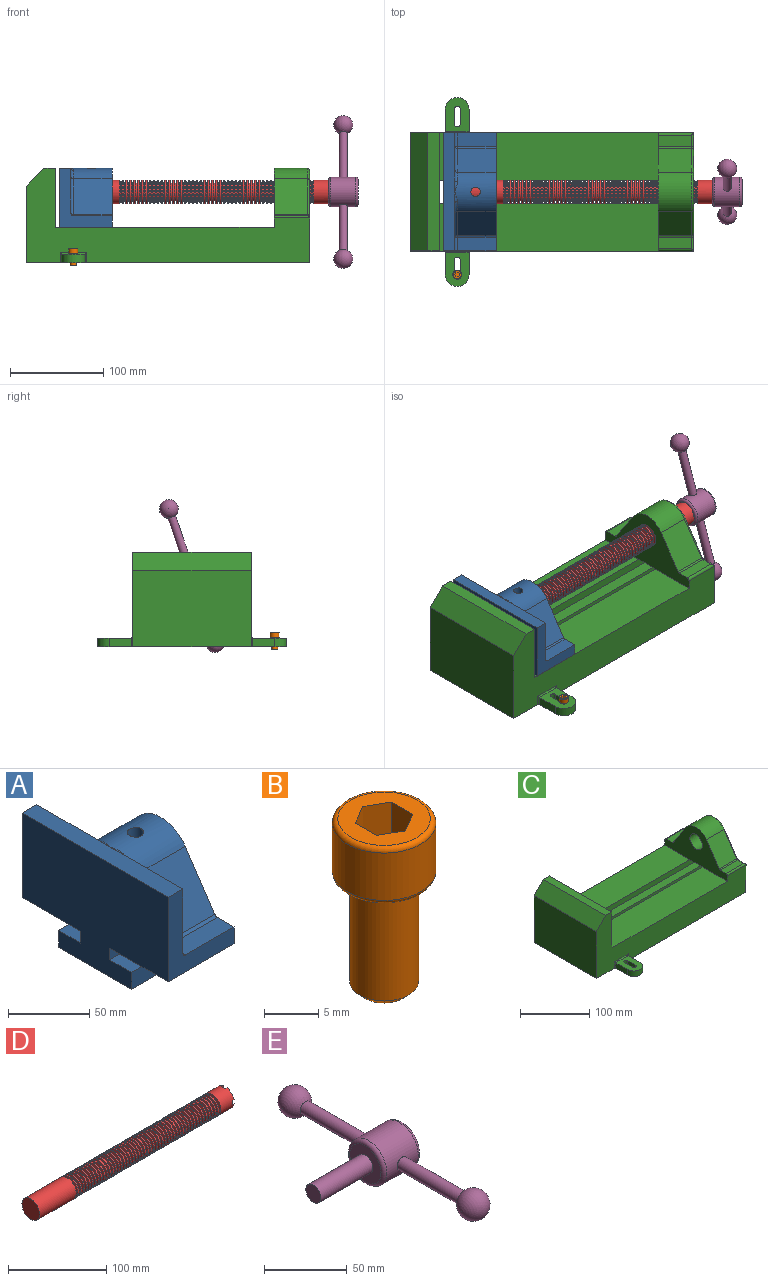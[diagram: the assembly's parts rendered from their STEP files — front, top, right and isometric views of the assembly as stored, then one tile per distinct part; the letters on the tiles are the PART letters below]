
ASSEMBLY  parts=5 mates=5
PART A: 36 faces, bbox 57.2x127x89 mm
  f0: plane 57.15x50.8mm, normal (0,0,-1), area 2903.2mm2, adj f6,f9,f10,f23
  f1: cylinder r=12.7mm len=44.45mm, axis (1,0,0), area 3464.3mm2, adj f6,f15,f16
  f2: plane 41.91x14.52mm, normal (0,0,1), area 608.5mm2, adj f6,f11,f24,f25
  f3: plane 51.86x48.26mm, normal (1,0,0), area 1495.7mm2, adj f8,f10,f31,f33,f35
  f4: plane 51.86x48.26mm, normal (1,0,0), area 1495.7mm2, adj f8,f11,f24,f28,f29
  f5: plane 57.15x50.8mm, normal (0,0,-1), area 2903.2mm2, adj f6,f9,f11,f22
  f6: plane 127x85.09mm, normal (1,0,0), area 5190.6mm2, adj f0,f1,f2,f5,f7,f10,f11,f12
  f7: plane 41.91x14.52mm, normal (0,0,1), area 608.5mm2, adj f6,f10,f30,f31
  f8: plane 127x12.7mm, normal (0,0,1), area 1612.9mm2, adj f3,f4,f9,f10,f11,f26,f34
  f9: plane 127x85.09mm, normal (-1,0,0), area 9096.8mm2, adj f0,f5,f8,f10,f11,f17,f18,f19
  f10: plane 63.5x57.15mm, normal (0,-1,0), area 1372.3mm2, adj f0,f3,f6,f7,f8,f9,f31
  f11: plane 63.5x57.15mm, normal (0,1,0), area 1372.3mm2, adj f2,f4,f5,f6,f8,f9,f24
  f12: plane 41.91x38.43mm, normal (0,-0.83,0.56), area 1939.2mm2, adj f6,f13,f30,f33
  f13: cylinder r=25.4mm len=44.45mm, axis (1,0,0), area 2026.5mm2, adj f6,f12,f14,f16,f26,f28,f34,f35
  f14: plane 41.91x38.43mm, normal (0,0.83,0.56), area 1939.2mm2, adj f6,f13,f25,f29
  f15: plane 25.4x25.4mm, normal (1,0,0), area 506.7mm2, adj f1
  f16: cylinder r=5.08mm len=13.76mm, axis (0,0,1), area 414mm2, adj f1,f13
  f17: plane 57.15x19.05mm, normal (0,0,1), area 1088.7mm2, adj f6,f9,f18,f23
  f18: plane 57.15x12.7mm, normal (0,-1,0), area 725.8mm2, adj f6,f9,f17,f19
  f19: plane 63.5x57.15mm, normal (0,0,-1), area 3629mm2, adj f6,f9,f18,f20
  f20: plane 57.15x12.7mm, normal (0,1,0), area 725.8mm2, adj f6,f9,f19,f21
  f21: plane 57.15x19.05mm, normal (0,0,1), area 1088.7mm2, adj f6,f9,f20,f22
  f22: plane 57.15x8.89mm, normal (0,1,0), area 508.1mm2, adj f5,f6,f9,f21
  f23: plane 57.15x8.89mm, normal (0,-1,0), area 508.1mm2, adj f0,f6,f9,f17
  f24: cylinder r=2.54mm len=14.52mm, axis (0,-1,0), area 57.9mm2, adj f2,f4,f11,f27
  f25: cylinder r=2.54mm len=41.91mm, axis (1,0,0), area 104.3mm2, adj f2,f6,f14,f27
  f26: bspline ~12.24x2.8mm, area 20.9mm2, adj f8,f13,f28
  f27: sphere r=2.54mm, area 6.3mm2, adj f24,f25,f29
  f28: torus R=27.94mm, axis (1,0,0), area 57.8mm2, adj f4,f13,f26,f29
  f29: cylinder r=2.54mm len=39.84mm, axis (0,-0.56,0.83), area 184.6mm2, adj f4,f14,f27,f28
  f30: cylinder r=2.54mm len=41.91mm, axis (1,0,0), area 104.3mm2, adj f6,f7,f12,f32
  f31: cylinder r=2.54mm len=14.52mm, axis (0,-1,0), area 57.9mm2, adj f3,f7,f10,f32
  f32: sphere r=2.54mm, area 6.3mm2, adj f30,f31,f33
  f33: cylinder r=2.54mm len=39.84mm, axis (0,-0.56,-0.83), area 184.6mm2, adj f3,f12,f32,f35
  f34: bspline ~12.24x2.8mm, area 20.9mm2, adj f8,f13,f35
  f35: torus R=27.94mm, axis (1,0,0), area 57.8mm2, adj f3,f13,f33,f34
PART B: 15 faces, bbox 10.3x10.3x19.1 mm
  f0: plane 8.51x8.51mm, normal (0,0,1), area 37.2mm2, adj f5,f6,f7,f8,f9,f10,f14
  f1: cylinder r=3.17mm len=11.94mm, axis (0,0,1), area 238.2mm2, adj f4,f12
  f2: plane 4.83x4.83mm, normal (0,0,-1), area 18.3mm2, adj f12
  f3: cylinder r=4.76mm len=9.53mm, axis (0,0,-1), area 159.6mm2, adj f13,f14
  f4: plane 8.51x8.51mm, normal (0,0,-1), area 25.2mm2, adj f1,f13
  f5: plane 4.83x2.38mm, normal (-0.5,-0.87,0), area 13.3mm2, adj f0,f6,f10,f11
  f6: plane 4.83x2.38mm, normal (0.5,-0.87,0), area 13.3mm2, adj f0,f5,f7,f11
  f7: plane 4.83x2.75mm, normal (1,0,0), area 13.3mm2, adj f0,f6,f8,f11
  f8: plane 4.83x2.38mm, normal (0.5,0.87,0), area 13.3mm2, adj f0,f7,f9,f11
  f9: plane 4.83x2.38mm, normal (-0.5,0.87,0), area 13.3mm2, adj f0,f8,f10,f11
  f10: plane 4.83x2.75mm, normal (-1,0,0), area 13.3mm2, adj f0,f5,f9,f11
  f11: plane 5.5x4.76mm, normal (0,0,1), area 19.6mm2, adj f5,f6,f7,f8,f9,f10
  f12: cone r=3.17mm half-angle=45deg, axis (0,0,1), area 18.9mm2, adj f1,f2
  f13: torus R=4.25mm, axis (0,0,1), area 23mm2, adj f3,f4
  f14: torus R=4.25mm, axis (0,0,1), area 23mm2, adj f0,f3
PART C: 61 faces, bbox 304.8x203.2x103.7 mm
  f0: plane 304.8x101.6mm, normal (0,1,0), area 13520.3mm2, adj f3,f4,f5,f6,f7,f8,f9,f16
  f1: plane 304.8x101.6mm, normal (0,-1,0), area 13520.3mm2, adj f2,f3,f5,f6,f7,f8,f9,f16
  f2: plane 234.95x50.8mm, normal (0,0,1), area 11935.5mm2, adj f1,f5,f16,f26
  f3: plane 127x99.06mm, normal (1,0,0), area 7097.5mm2, adj f0,f1,f9,f14,f17,f18,f19,f20
  f4: plane 234.95x50.8mm, normal (0,0,1), area 11935.5mm2, adj f0,f5,f16,f27
  f5: plane 127x101.6mm, normal (1,0,0), area 9516.1mm2, adj f0,f1,f2,f4,f6,f9,f18,f19
  f6: plane 127x12.7mm, normal (0,0,1), area 1612.9mm2, adj f0,f1,f5,f7
  f7: plane 127x19.05mm, normal (-0.71,0,0.71), area 3421.5mm2, adj f0,f1,f6,f8
  f8: plane 127x82.55mm, normal (-1,0,0), area 10483.8mm2, adj f0,f1,f7,f9
  f9: plane 304.8x203.2mm, normal (0,0,-1), area 33298.3mm2, adj f0,f1,f3,f5,f8,f21,f22,f39
  f10: plane 35.56x11.98mm, normal (0,0,1), area 426mm2, adj f16,f28,f29,f30
  f11: plane 38.43x35.56mm, normal (0,0.83,0.56), area 1645.4mm2, adj f12,f16,f29,f32
  f12: cylinder r=25.4mm len=42.19mm, axis (1,0,0), area 1770.2mm2, adj f11,f13,f16,f33
  f13: plane 38.43x35.56mm, normal (0,-0.83,0.56), area 1645.4mm2, adj f12,f16,f34,f35
  f14: cylinder r=12.7mm len=38.1mm, axis (1,0,0), area 3040.2mm2, adj f3,f16
  f15: plane 35.56x11.98mm, normal (0,0,1), area 426mm2, adj f16,f34,f36,f38
  f16: plane 127x63.5mm, normal (-1,0,0), area 4155.5mm2, adj f0,f1,f2,f4,f10,f11,f12,f13
  f17: plane 38.1x25.4mm, normal (0,0,-1), area 967.7mm2, adj f3,f16,f26,f27
  f18: plane 273.05x19.05mm, normal (0,0,-1), area 5201.6mm2, adj f3,f5,f19,f26
  f19: plane 273.05x12.7mm, normal (0,1,0), area 3467.7mm2, adj f3,f5,f18,f20
  f20: plane 273.05x19.05mm, normal (0,0,1), area 5201.6mm2, adj f3,f5,f19,f21
  f21: plane 273.05x16.51mm, normal (0,1,0), area 4508.1mm2, adj f3,f5,f9,f20
  f22: plane 273.05x16.51mm, normal (0,-1,0), area 4508.1mm2, adj f3,f5,f9,f23
  f23: plane 273.05x19.05mm, normal (0,0,1), area 5201.6mm2, adj f3,f5,f22,f24
  f24: plane 273.05x12.7mm, normal (0,-1,0), area 3467.7mm2, adj f3,f5,f23,f25
  f25: plane 273.05x19.05mm, normal (0,0,-1), area 5201.6mm2, adj f3,f5,f24,f27
  f26: plane 273.05x8.89mm, normal (0,1,0), area 2427.4mm2, adj f2,f3,f5,f17,f18
  f27: plane 273.05x8.89mm, normal (0,-1,0), area 2427.4mm2, adj f3,f4,f5,f17,f25
  f28: cylinder r=2.54mm len=38.1mm, axis (1,0,0), area 148.3mm2, adj f0,f10,f16,f30
  f29: cylinder r=2.54mm len=35.56mm, axis (-1,0,0), area 88.5mm2, adj f10,f11,f16,f31
  f30: cylinder r=2.54mm len=14.52mm, axis (0,1,0), area 54.3mm2, adj f3,f10,f28,f31
  f31: torus R=5.08mm, axis (-1,0,0), area 13.5mm2, adj f3,f29,f30,f32
  f32: cylinder r=2.54mm len=39.84mm, axis (0,0.56,-0.83), area 184.6mm2, adj f3,f11,f31,f33
  f33: torus R=22.86mm, axis (-1,0,0), area 191.4mm2, adj f3,f12,f32,f35
  f34: cylinder r=2.54mm len=35.56mm, axis (-1,0,0), area 88.5mm2, adj f13,f15,f16,f37
  f35: cylinder r=2.54mm len=39.84mm, axis (0,0.56,0.83), area 184.6mm2, adj f3,f13,f33,f37
  f36: cylinder r=2.54mm len=38.1mm, axis (-1,0,0), area 148.3mm2, adj f1,f15,f16,f38
  f37: torus R=5.08mm, axis (-1,0,0), area 13.5mm2, adj f3,f34,f35,f38
  f38: cylinder r=2.54mm len=14.52mm, axis (0,1,0), area 54.3mm2, adj f3,f15,f36,f37
  f39: plane 23.88x9.53mm, normal (-1,0,0), area 227.4mm2, adj f9,f45,f46,f60
  f40: plane 23.88x9.53mm, normal (1,0,0), area 227.4mm2, adj f9,f45,f46,f58
  f41: cylinder r=3.3mm len=9.53mm, axis (0,0,-1), area 98.8mm2, adj f9,f42,f44,f46
  f42: plane 15.62x9.53mm, normal (-1,0,0), area 148.8mm2, adj f9,f41,f43,f46
  f43: cylinder r=3.3mm len=9.53mm, axis (0,0,-1), area 98.8mm2, adj f9,f42,f44,f46
  f44: plane 15.62x9.53mm, normal (1,0,0), area 148.8mm2, adj f9,f41,f43,f46
  f45: cylinder r=12.7mm len=25.4mm, axis (0,0,-1), area 380mm2, adj f9,f39,f40,f46
  f46: plane 36.58x25.4mm, normal (0,0,1), area 722.4mm2, adj f39,f40,f41,f42,f43,f44,f45,f59
  f47: plane 23.88x9.53mm, normal (-1,0,0), area 227.4mm2, adj f9,f53,f54,f56
  f48: plane 23.88x9.53mm, normal (1,0,0), area 227.4mm2, adj f9,f53,f54,f55
  f49: cylinder r=3.3mm len=9.53mm, axis (0,0,-1), area 98.8mm2, adj f9,f50,f52,f54
  f50: plane 15.62x9.53mm, normal (-1,0,0), area 148.8mm2, adj f9,f49,f51,f54
  f51: cylinder r=3.3mm len=9.53mm, axis (0,0,-1), area 98.8mm2, adj f9,f50,f52,f54
  f52: plane 15.62x9.53mm, normal (1,0,0), area 148.8mm2, adj f9,f49,f51,f54
  f53: cylinder r=12.7mm len=25.4mm, axis (0,0,-1), area 380mm2, adj f9,f47,f48,f54
  f54: plane 36.58x25.4mm, normal (0,0,1), area 722.4mm2, adj f47,f48,f49,f50,f51,f52,f53,f57
  f55: cylinder r=1.52mm len=11.05mm, axis (0,0,-1), area 24.1mm2, adj f0,f9,f48,f57
  f56: cylinder r=1.52mm len=11.05mm, axis (0,0,1), area 24.1mm2, adj f0,f9,f47,f57
  f57: cylinder r=1.52mm len=28.45mm, axis (1,0,0), area 63.5mm2, adj f0,f54,f55,f56
  f58: cylinder r=1.52mm len=11.05mm, axis (0,0,1), area 24.1mm2, adj f1,f9,f40,f59
  f59: cylinder r=1.52mm len=28.45mm, axis (-1,0,0), area 63.5mm2, adj f1,f46,f58,f60
  f60: cylinder r=1.52mm len=11.05mm, axis (0,0,-1), area 24.1mm2, adj f1,f9,f39,f59
PART D: 220 faces, bbox 279.4x25.4x25.4 mm
  f0: cylinder r=12.7mm len=25.4mm, axis (-1,0,0), area 1468.2mm2, adj f1,f2,f3,f5,f7,f208,f209,f210
  f1: plane 9.9x9.9mm, normal (1,0,0), area 62.3mm2, adj f0,f4,f213,f216
  f2: plane 9.9x9.9mm, normal (1,0,0), area 62.3mm2, adj f0,f4,f210,f218
  f3: plane 9.9x9.9mm, normal (1,0,0), area 62.3mm2, adj f0,f4,f209,f212
  f4: cylinder r=6.35mm len=25.4mm, axis (1,0,0), area 960.3mm2, adj f1,f2,f3,f5,f6,f208,f209,f210
  f5: plane 9.9x9.9mm, normal (1,0,0), area 62.3mm2, adj f0,f4,f215,f217
  f6: plane 12.7x12.7mm, normal (1,0,0), area 126.7mm2, adj f4
  f7: cone r=12.7mm half-angle=76deg, axis (1,0,0), area 188mm2, adj f0,f9
  f8: cone r=10.16mm half-angle=76deg, axis (-1,0,0), area 188mm2, adj f9,f10
  f9: cylinder r=10.16mm len=20.32mm, axis (1,0,0), area 81.1mm2, adj f7,f8
  f10: cylinder r=12.7mm len=25.4mm, axis (-1,0,0), area 131.7mm2, adj f8,f11
  f11: cone r=12.7mm half-angle=76deg, axis (1,0,0), area 188mm2, adj f10,f13
  f12: cone r=10.16mm half-angle=76deg, axis (-1,0,0), area 188mm2, adj f13,f14
  f13: cylinder r=10.16mm len=20.32mm, axis (1,0,0), area 81.1mm2, adj f11,f12
  f14: cylinder r=12.7mm len=25.4mm, axis (-1,0,0), area 131.7mm2, adj f12,f15
  f15: cone r=12.7mm half-angle=76deg, axis (1,0,0), area 188mm2, adj f14,f17
  f16: cone r=10.16mm half-angle=76deg, axis (-1,0,0), area 188mm2, adj f17,f18
  f17: cylinder r=10.16mm len=20.32mm, axis (1,0,0), area 81.1mm2, adj f15,f16
  f18: cylinder r=12.7mm len=25.4mm, axis (-1,0,0), area 131.7mm2, adj f16,f19
  f19: cone r=12.7mm half-angle=76deg, axis (1,0,0), area 188mm2, adj f18,f21
  f20: cone r=10.16mm half-angle=76deg, axis (-1,0,0), area 188mm2, adj f21,f22
  f21: cylinder r=10.16mm len=20.32mm, axis (1,0,0), area 81.1mm2, adj f19,f20
  f22: cylinder r=12.7mm len=25.4mm, axis (-1,0,0), area 131.7mm2, adj f20,f23
  f23: cone r=12.7mm half-angle=76deg, axis (1,0,0), area 188mm2, adj f22,f25
  f24: cone r=10.16mm half-angle=76deg, axis (-1,0,0), area 188mm2, adj f25,f26
  f25: cylinder r=10.16mm len=20.32mm, axis (1,0,0), area 81.1mm2, adj f23,f24
  f26: cylinder r=12.7mm len=25.4mm, axis (-1,0,0), area 131.7mm2, adj f24,f27
  f27: cone r=12.7mm half-angle=76deg, axis (1,0,0), area 188mm2, adj f26,f29
  f28: cone r=10.16mm half-angle=76deg, axis (-1,0,0), area 188mm2, adj f29,f30
  f29: cylinder r=10.16mm len=20.32mm, axis (1,0,0), area 81.1mm2, adj f27,f28
  f30: cylinder r=12.7mm len=25.4mm, axis (-1,0,0), area 131.7mm2, adj f28,f31
  f31: cone r=12.7mm half-angle=76deg, axis (1,0,0), area 188mm2, adj f30,f33
  f32: cone r=10.16mm half-angle=76deg, axis (-1,0,0), area 188mm2, adj f33,f34
  f33: cylinder r=10.16mm len=20.32mm, axis (1,0,0), area 81.1mm2, adj f31,f32
  f34: cylinder r=12.7mm len=25.4mm, axis (-1,0,0), area 131.7mm2, adj f32,f35
  f35: cone r=12.7mm half-angle=76deg, axis (1,0,0), area 188mm2, adj f34,f37
  f36: cone r=10.16mm half-angle=76deg, axis (-1,0,0), area 188mm2, adj f37,f38
  f37: cylinder r=10.16mm len=20.32mm, axis (1,0,0), area 81.1mm2, adj f35,f36
  f38: cylinder r=12.7mm len=25.4mm, axis (-1,0,0), area 131.7mm2, adj f36,f39
  f39: cone r=12.7mm half-angle=76deg, axis (1,0,0), area 188mm2, adj f38,f41
  f40: cone r=10.16mm half-angle=76deg, axis (-1,0,0), area 188mm2, adj f41,f42
  f41: cylinder r=10.16mm len=20.32mm, axis (1,0,0), area 81.1mm2, adj f39,f40
  f42: cylinder r=12.7mm len=25.4mm, axis (-1,0,0), area 131.7mm2, adj f40,f43
  f43: cone r=12.7mm half-angle=76deg, axis (1,0,0), area 188mm2, adj f42,f45
  f44: cone r=10.16mm half-angle=76deg, axis (-1,0,0), area 188mm2, adj f45,f46
  f45: cylinder r=10.16mm len=20.32mm, axis (1,0,0), area 81.1mm2, adj f43,f44
  f46: cylinder r=12.7mm len=25.4mm, axis (-1,0,0), area 131.7mm2, adj f44,f47
  f47: cone r=12.7mm half-angle=76deg, axis (1,0,0), area 188mm2, adj f46,f49
  f48: cone r=10.16mm half-angle=76deg, axis (-1,0,0), area 188mm2, adj f49,f50
  f49: cylinder r=10.16mm len=20.32mm, axis (1,0,0), area 81.1mm2, adj f47,f48
  f50: cylinder r=12.7mm len=25.4mm, axis (-1,0,0), area 131.7mm2, adj f48,f51
  f51: cone r=12.7mm half-angle=76deg, axis (1,0,0), area 188mm2, adj f50,f53
  f52: cone r=10.16mm half-angle=76deg, axis (-1,0,0), area 188mm2, adj f53,f54
  f53: cylinder r=10.16mm len=20.32mm, axis (1,0,0), area 81.1mm2, adj f51,f52
  f54: cylinder r=12.7mm len=25.4mm, axis (-1,0,0), area 131.7mm2, adj f52,f55
  f55: cone r=12.7mm half-angle=76deg, axis (1,0,0), area 188mm2, adj f54,f57
  f56: cone r=10.16mm half-angle=76deg, axis (-1,0,0), area 188mm2, adj f57,f58
  f57: cylinder r=10.16mm len=20.32mm, axis (1,0,0), area 81.1mm2, adj f55,f56
  f58: cylinder r=12.7mm len=25.4mm, axis (-1,0,0), area 131.7mm2, adj f56,f59
  f59: cone r=12.7mm half-angle=76deg, axis (1,0,0), area 188mm2, adj f58,f61
  f60: cone r=10.16mm half-angle=76deg, axis (-1,0,0), area 188mm2, adj f61,f62
  f61: cylinder r=10.16mm len=20.32mm, axis (1,0,0), area 81.1mm2, adj f59,f60
  f62: cylinder r=12.7mm len=25.4mm, axis (-1,0,0), area 131.7mm2, adj f60,f63
  f63: cone r=12.7mm half-angle=76deg, axis (1,0,0), area 188mm2, adj f62,f65
  f64: cone r=10.16mm half-angle=76deg, axis (-1,0,0), area 188mm2, adj f65,f66
  f65: cylinder r=10.16mm len=20.32mm, axis (1,0,0), area 81.1mm2, adj f63,f64
  f66: cylinder r=12.7mm len=25.4mm, axis (-1,0,0), area 131.7mm2, adj f64,f67
  f67: cone r=12.7mm half-angle=76deg, axis (1,0,0), area 188mm2, adj f66,f69
  f68: cone r=10.16mm half-angle=76deg, axis (-1,0,0), area 188mm2, adj f69,f70
  f69: cylinder r=10.16mm len=20.32mm, axis (1,0,0), area 81.1mm2, adj f67,f68
  f70: cylinder r=12.7mm len=25.4mm, axis (-1,0,0), area 131.7mm2, adj f68,f71
  f71: cone r=12.7mm half-angle=76deg, axis (1,0,0), area 188mm2, adj f70,f73
  f72: cone r=10.16mm half-angle=76deg, axis (-1,0,0), area 188mm2, adj f73,f74
  f73: cylinder r=10.16mm len=20.32mm, axis (1,0,0), area 81.1mm2, adj f71,f72
  f74: cylinder r=12.7mm len=25.4mm, axis (-1,0,0), area 131.7mm2, adj f72,f75
  f75: cone r=12.7mm half-angle=76deg, axis (1,0,0), area 188mm2, adj f74,f77
  f76: cone r=10.16mm half-angle=76deg, axis (-1,0,0), area 188mm2, adj f77,f78
  f77: cylinder r=10.16mm len=20.32mm, axis (1,0,0), area 81.1mm2, adj f75,f76
  f78: cylinder r=12.7mm len=25.4mm, axis (-1,0,0), area 131.7mm2, adj f76,f79
  f79: cone r=12.7mm half-angle=76deg, axis (1,0,0), area 188mm2, adj f78,f81
  f80: cone r=10.16mm half-angle=76deg, axis (-1,0,0), area 188mm2, adj f81,f82
  f81: cylinder r=10.16mm len=20.32mm, axis (1,0,0), area 81.1mm2, adj f79,f80
  f82: cylinder r=12.7mm len=25.4mm, axis (-1,0,0), area 131.7mm2, adj f80,f83
  f83: cone r=12.7mm half-angle=76deg, axis (1,0,0), area 188mm2, adj f82,f85
  f84: cone r=10.16mm half-angle=76deg, axis (-1,0,0), area 188mm2, adj f85,f86
  f85: cylinder r=10.16mm len=20.32mm, axis (1,0,0), area 81.1mm2, adj f83,f84
  f86: cylinder r=12.7mm len=25.4mm, axis (-1,0,0), area 131.7mm2, adj f84,f87
  f87: cone r=12.7mm half-angle=76deg, axis (1,0,0), area 188mm2, adj f86,f89
  f88: cone r=10.16mm half-angle=76deg, axis (-1,0,0), area 188mm2, adj f89,f90
  f89: cylinder r=10.16mm len=20.32mm, axis (1,0,0), area 81.1mm2, adj f87,f88
  f90: cylinder r=12.7mm len=25.4mm, axis (-1,0,0), area 131.7mm2, adj f88,f91
  f91: cone r=12.7mm half-angle=76deg, axis (1,0,0), area 188mm2, adj f90,f93
  f92: cone r=10.16mm half-angle=76deg, axis (-1,0,0), area 188mm2, adj f93,f94
  f93: cylinder r=10.16mm len=20.32mm, axis (1,0,0), area 81.1mm2, adj f91,f92
  f94: cylinder r=12.7mm len=25.4mm, axis (-1,0,0), area 131.7mm2, adj f92,f95
  f95: cone r=12.7mm half-angle=76deg, axis (1,0,0), area 188mm2, adj f94,f97
  f96: cone r=10.16mm half-angle=76deg, axis (-1,0,0), area 188mm2, adj f97,f98
  f97: cylinder r=10.16mm len=20.32mm, axis (1,0,0), area 81.1mm2, adj f95,f96
  f98: cylinder r=12.7mm len=25.4mm, axis (-1,0,0), area 131.7mm2, adj f96,f99
  f99: cone r=12.7mm half-angle=76deg, axis (1,0,0), area 188mm2, adj f98,f101
  f100: cone r=10.16mm half-angle=76deg, axis (-1,0,0), area 188mm2, adj f101,f102
  f101: cylinder r=10.16mm len=20.32mm, axis (1,0,0), area 81.1mm2, adj f99,f100
  f102: cylinder r=12.7mm len=25.4mm, axis (-1,0,0), area 131.7mm2, adj f100,f103
  f103: cone r=12.7mm half-angle=76deg, axis (1,0,0), area 188mm2, adj f102,f105
  f104: cone r=10.16mm half-angle=76deg, axis (-1,0,0), area 188mm2, adj f105,f106
  f105: cylinder r=10.16mm len=20.32mm, axis (1,0,0), area 81.1mm2, adj f103,f104
  f106: cylinder r=12.7mm len=25.4mm, axis (-1,0,0), area 131.7mm2, adj f104,f107
  f107: cone r=12.7mm half-angle=76deg, axis (1,0,0), area 188mm2, adj f106,f109
  f108: cone r=10.16mm half-angle=76deg, axis (-1,0,0), area 188mm2, adj f109,f110
  f109: cylinder r=10.16mm len=20.32mm, axis (1,0,0), area 81.1mm2, adj f107,f108
  f110: cylinder r=12.7mm len=25.4mm, axis (-1,0,0), area 131.7mm2, adj f108,f111
  f111: cone r=12.7mm half-angle=76deg, axis (1,0,0), area 188mm2, adj f110,f113
  f112: cone r=10.16mm half-angle=76deg, axis (-1,0,0), area 188mm2, adj f113,f114
  f113: cylinder r=10.16mm len=20.32mm, axis (1,0,0), area 81.1mm2, adj f111,f112
  f114: cylinder r=12.7mm len=25.4mm, axis (-1,0,0), area 131.7mm2, adj f112,f115
  f115: cone r=12.7mm half-angle=76deg, axis (1,0,0), area 188mm2, adj f114,f117
  f116: cone r=10.16mm half-angle=76deg, axis (-1,0,0), area 188mm2, adj f117,f118
  f117: cylinder r=10.16mm len=20.32mm, axis (1,0,0), area 81.1mm2, adj f115,f116
  f118: cylinder r=12.7mm len=25.4mm, axis (-1,0,0), area 131.7mm2, adj f116,f119
  f119: cone r=12.7mm half-angle=76deg, axis (1,0,0), area 188mm2, adj f118,f121
  f120: cone r=10.16mm half-angle=76deg, axis (-1,0,0), area 188mm2, adj f121,f122
  f121: cylinder r=10.16mm len=20.32mm, axis (1,0,0), area 81.1mm2, adj f119,f120
  f122: cylinder r=12.7mm len=25.4mm, axis (-1,0,0), area 131.7mm2, adj f120,f123
  f123: cone r=12.7mm half-angle=76deg, axis (1,0,0), area 188mm2, adj f122,f125
  f124: cone r=10.16mm half-angle=76deg, axis (-1,0,0), area 188mm2, adj f125,f126
  f125: cylinder r=10.16mm len=20.32mm, axis (1,0,0), area 81.1mm2, adj f123,f124
  f126: cylinder r=12.7mm len=25.4mm, axis (-1,0,0), area 131.7mm2, adj f124,f127
  f127: cone r=12.7mm half-angle=76deg, axis (1,0,0), area 188mm2, adj f126,f129
  f128: cone r=10.16mm half-angle=76deg, axis (-1,0,0), area 188mm2, adj f129,f130
  f129: cylinder r=10.16mm len=20.32mm, axis (1,0,0), area 81.1mm2, adj f127,f128
  f130: cylinder r=12.7mm len=25.4mm, axis (-1,0,0), area 131.7mm2, adj f128,f131
  f131: cone r=12.7mm half-angle=76deg, axis (1,0,0), area 188mm2, adj f130,f133
  f132: cone r=10.16mm half-angle=76deg, axis (-1,0,0), area 188mm2, adj f133,f134
  f133: cylinder r=10.16mm len=20.32mm, axis (1,0,0), area 81.1mm2, adj f131,f132
  f134: cylinder r=12.7mm len=25.4mm, axis (-1,0,0), area 131.7mm2, adj f132,f135
  f135: cone r=12.7mm half-angle=76deg, axis (1,0,0), area 188mm2, adj f134,f137
  f136: cone r=10.16mm half-angle=76deg, axis (-1,0,0), area 188mm2, adj f137,f138
  f137: cylinder r=10.16mm len=20.32mm, axis (1,0,0), area 81.1mm2, adj f135,f136
  f138: cylinder r=12.7mm len=25.4mm, axis (-1,0,0), area 131.7mm2, adj f136,f139
  f139: cone r=12.7mm half-angle=76deg, axis (1,0,0), area 188mm2, adj f138,f141
  f140: cone r=10.16mm half-angle=76deg, axis (-1,0,0), area 188mm2, adj f141,f142
  f141: cylinder r=10.16mm len=20.32mm, axis (1,0,0), area 81.1mm2, adj f139,f140
  f142: cylinder r=12.7mm len=25.4mm, axis (-1,0,0), area 131.7mm2, adj f140,f143
  f143: cone r=12.7mm half-angle=76deg, axis (1,0,0), area 188mm2, adj f142,f145
  f144: cone r=10.16mm half-angle=76deg, axis (-1,0,0), area 188mm2, adj f145,f146
  f145: cylinder r=10.16mm len=20.32mm, axis (1,0,0), area 81.1mm2, adj f143,f144
  f146: cylinder r=12.7mm len=25.4mm, axis (-1,0,0), area 131.7mm2, adj f144,f147
  f147: cone r=12.7mm half-angle=76deg, axis (1,0,0), area 188mm2, adj f146,f149
  f148: cone r=10.16mm half-angle=76deg, axis (-1,0,0), area 188mm2, adj f149,f150
  f149: cylinder r=10.16mm len=20.32mm, axis (1,0,0), area 81.1mm2, adj f147,f148
  f150: cylinder r=12.7mm len=25.4mm, axis (-1,0,0), area 131.7mm2, adj f148,f151
  f151: cone r=12.7mm half-angle=76deg, axis (1,0,0), area 188mm2, adj f150,f153
  f152: cone r=10.16mm half-angle=76deg, axis (-1,0,0), area 188mm2, adj f153,f154
  f153: cylinder r=10.16mm len=20.32mm, axis (1,0,0), area 81.1mm2, adj f151,f152
  f154: cylinder r=12.7mm len=25.4mm, axis (-1,0,0), area 131.7mm2, adj f152,f155
  f155: cone r=12.7mm half-angle=76deg, axis (1,0,0), area 188mm2, adj f154,f157
  f156: cone r=10.16mm half-angle=76deg, axis (-1,0,0), area 188mm2, adj f157,f158
  f157: cylinder r=10.16mm len=20.32mm, axis (1,0,0), area 81.1mm2, adj f155,f156
  f158: cylinder r=12.7mm len=25.4mm, axis (-1,0,0), area 131.7mm2, adj f156,f159
  f159: cone r=12.7mm half-angle=76deg, axis (1,0,0), area 188mm2, adj f158,f161
  f160: cone r=10.16mm half-angle=76deg, axis (-1,0,0), area 188mm2, adj f161,f162
  f161: cylinder r=10.16mm len=20.32mm, axis (1,0,0), area 81.1mm2, adj f159,f160
  f162: cylinder r=12.7mm len=25.4mm, axis (-1,0,0), area 131.7mm2, adj f160,f163
  f163: cone r=12.7mm half-angle=76deg, axis (1,0,0), area 188mm2, adj f162,f165
  f164: cone r=10.16mm half-angle=76deg, axis (-1,0,0), area 188mm2, adj f165,f166
  f165: cylinder r=10.16mm len=20.32mm, axis (1,0,0), area 81.1mm2, adj f163,f164
  f166: cylinder r=12.7mm len=25.4mm, axis (-1,0,0), area 131.7mm2, adj f164,f167
  f167: cone r=12.7mm half-angle=76deg, axis (1,0,0), area 188mm2, adj f166,f169
  f168: cone r=10.16mm half-angle=76deg, axis (-1,0,0), area 188mm2, adj f169,f170
  f169: cylinder r=10.16mm len=20.32mm, axis (1,0,0), area 81.1mm2, adj f167,f168
  f170: cylinder r=12.7mm len=25.4mm, axis (-1,0,0), area 131.7mm2, adj f168,f171
  f171: cone r=12.7mm half-angle=76deg, axis (1,0,0), area 188mm2, adj f170,f173
  f172: cone r=10.16mm half-angle=76deg, axis (-1,0,0), area 188mm2, adj f173,f174
  f173: cylinder r=10.16mm len=20.32mm, axis (1,0,0), area 81.1mm2, adj f171,f172
  f174: cylinder r=12.7mm len=25.4mm, axis (-1,0,0), area 131.7mm2, adj f172,f175
  f175: cone r=12.7mm half-angle=76deg, axis (1,0,0), area 188mm2, adj f174,f177
  f176: cone r=10.16mm half-angle=76deg, axis (-1,0,0), area 188mm2, adj f177,f178
  f177: cylinder r=10.16mm len=20.32mm, axis (1,0,0), area 81.1mm2, adj f175,f176
  f178: cylinder r=12.7mm len=25.4mm, axis (-1,0,0), area 131.7mm2, adj f176,f179
  f179: cone r=12.7mm half-angle=76deg, axis (1,0,0), area 188mm2, adj f178,f181
  f180: cone r=10.16mm half-angle=76deg, axis (-1,0,0), area 188mm2, adj f181,f182
  f181: cylinder r=10.16mm len=20.32mm, axis (1,0,0), area 81.1mm2, adj f179,f180
  f182: cylinder r=12.7mm len=25.4mm, axis (-1,0,0), area 131.7mm2, adj f180,f183
  f183: cone r=12.7mm half-angle=76deg, axis (1,0,0), area 188mm2, adj f182,f185
  f184: cone r=10.16mm half-angle=76deg, axis (-1,0,0), area 188mm2, adj f185,f186
  f185: cylinder r=10.16mm len=20.32mm, axis (1,0,0), area 81.1mm2, adj f183,f184
  f186: cylinder r=12.7mm len=25.4mm, axis (-1,0,0), area 131.7mm2, adj f184,f187
  f187: cone r=12.7mm half-angle=76deg, axis (1,0,0), area 188mm2, adj f186,f189
  f188: cone r=10.16mm half-angle=76deg, axis (-1,0,0), area 188mm2, adj f189,f190
  f189: cylinder r=10.16mm len=20.32mm, axis (1,0,0), area 81.1mm2, adj f187,f188
  f190: cylinder r=12.7mm len=25.4mm, axis (-1,0,0), area 131.7mm2, adj f188,f191
  f191: cone r=12.7mm half-angle=76deg, axis (1,0,0), area 188mm2, adj f190,f193
  f192: cone r=10.16mm half-angle=76deg, axis (-1,0,0), area 188mm2, adj f193,f194
  f193: cylinder r=10.16mm len=20.32mm, axis (1,0,0), area 81.1mm2, adj f191,f192
  f194: cylinder r=12.7mm len=25.4mm, axis (-1,0,0), area 131.7mm2, adj f192,f195
  f195: cone r=12.7mm half-angle=76deg, axis (1,0,0), area 188mm2, adj f194,f197
  f196: cone r=10.16mm half-angle=76deg, axis (-1,0,0), area 188mm2, adj f197,f198
  f197: cylinder r=10.16mm len=20.32mm, axis (1,0,0), area 81.1mm2, adj f195,f196
  f198: cylinder r=12.7mm len=25.4mm, axis (-1,0,0), area 131.7mm2, adj f196,f199
  f199: cone r=12.7mm half-angle=76deg, axis (1,0,0), area 188mm2, adj f198,f201
  f200: cone r=10.16mm half-angle=76deg, axis (-1,0,0), area 188mm2, adj f201,f202
  f201: cylinder r=10.16mm len=20.32mm, axis (1,0,0), area 81.1mm2, adj f199,f200
  f202: cylinder r=12.7mm len=25.4mm, axis (-1,0,0), area 131.7mm2, adj f200,f203
  f203: cone r=12.7mm half-angle=76deg, axis (1,0,0), area 188mm2, adj f202,f205
  f204: cone r=10.16mm half-angle=76deg, axis (-1,0,0), area 188mm2, adj f205,f207
  f205: cylinder r=10.16mm len=20.32mm, axis (1,0,0), area 81.1mm2, adj f203,f204
  f206: plane 25.4x25.4mm, normal (-1,0,0), area 506.7mm2, adj f207
  f207: cylinder r=12.7mm len=52.45mm, axis (-1,0,0), area 4185.4mm2, adj f204,f206
  f208: plane 6.88x5.08mm, normal (1,0,0), area 32.7mm2, adj f0,f4,f209,f210
  f209: plane 6.62x2.54mm, normal (0,-1,0), area 16.8mm2, adj f0,f3,f4,f208
  f210: plane 6.62x2.54mm, normal (0,1,0), area 16.8mm2, adj f0,f2,f4,f208
  f211: plane 6.88x5.08mm, normal (1,0,0), area 32.7mm2, adj f0,f4,f212,f213
  f212: plane 6.62x2.54mm, normal (0,0,1), area 16.8mm2, adj f0,f3,f4,f211
  f213: plane 6.62x2.54mm, normal (0,0,-1), area 16.8mm2, adj f0,f1,f4,f211
  f214: plane 6.88x5.08mm, normal (1,0,0), area 32.7mm2, adj f0,f4,f215,f216
  f215: plane 6.62x2.54mm, normal (0,1,0), area 16.8mm2, adj f0,f4,f5,f214
  f216: plane 6.62x2.54mm, normal (0,-1,0), area 16.8mm2, adj f0,f1,f4,f214
  f217: plane 6.62x2.54mm, normal (0,0,-1), area 16.8mm2, adj f0,f4,f5,f219
  f218: plane 6.62x2.54mm, normal (0,0,1), area 16.8mm2, adj f0,f2,f4,f219
  f219: plane 6.88x5.08mm, normal (1,0,0), area 32.7mm2, adj f0,f4,f217,f218
PART E: 11 faces, bbox 76.2x172.7x34.4 mm
  f0: sphere r=10.16mm, area 1231.8mm2, adj f1
  f1: cylinder r=4.45mm len=51.82mm, axis (0,1,0), area 1438.5mm2, adj f0,f4
  f2: sphere r=10.16mm, area 1231.8mm2, adj f3
  f3: cylinder r=4.45mm len=51.82mm, axis (0,1,0), area 1438.5mm2, adj f2,f4
  f4: cylinder r=15.88mm len=31.75mm, axis (-1,0,0), area 2534.7mm2, adj f1,f3,f9,f10
  f5: cylinder r=6.35mm len=44.45mm, axis (-1,0,0), area 1773.5mm2, adj f6,f8
  f6: plane 12.7x12.7mm, normal (-1,0,0), area 126.7mm2, adj f5
  f7: plane 26.67x26.67mm, normal (1,0,0), area 558.6mm2, adj f10
  f8: plane 26.67x26.67mm, normal (-1,0,0), area 432mm2, adj f5,f9
  f9: torus R=13.33mm, axis (1,0,0), area 374.8mm2, adj f4,f8
  f10: torus R=13.33mm, axis (1,0,0), area 374.8mm2, adj f4,f7
PLACE A t=(3.85,0,0)mm
PLACE B rot(axis=(0,0,1),90deg) t=(-254,-88.9,9.52)mm
PLACE C at identity fixed
PLACE D rot(axis=(1,0,0),71deg) t=(3.85,72.03,51.33)mm
PLACE E rot(axis=(1,0,0),71deg) t=(-17.74,72.03,51.33)mm
MATE fastened D.f4 <-> E.f5  axis (1,0,0) through (20.36,0,76.2)mm
MATE planar A.f0 <-> C.f2  axis (0,0,-1) through (-240.63,-38.1,38.1)mm
MATE pin_slot B.f1 <-> C.f41  axis (0,0,1) through (-254,-88.9,9.52)mm
MATE revolute D.f7 <-> A.f28  axis (-1,0,0) through (-256.5,0,76.2)mm
MATE cylindrical C.f12 <-> D.f7  axis (-1,0,0) through (-38.1,0,76.2)mm
